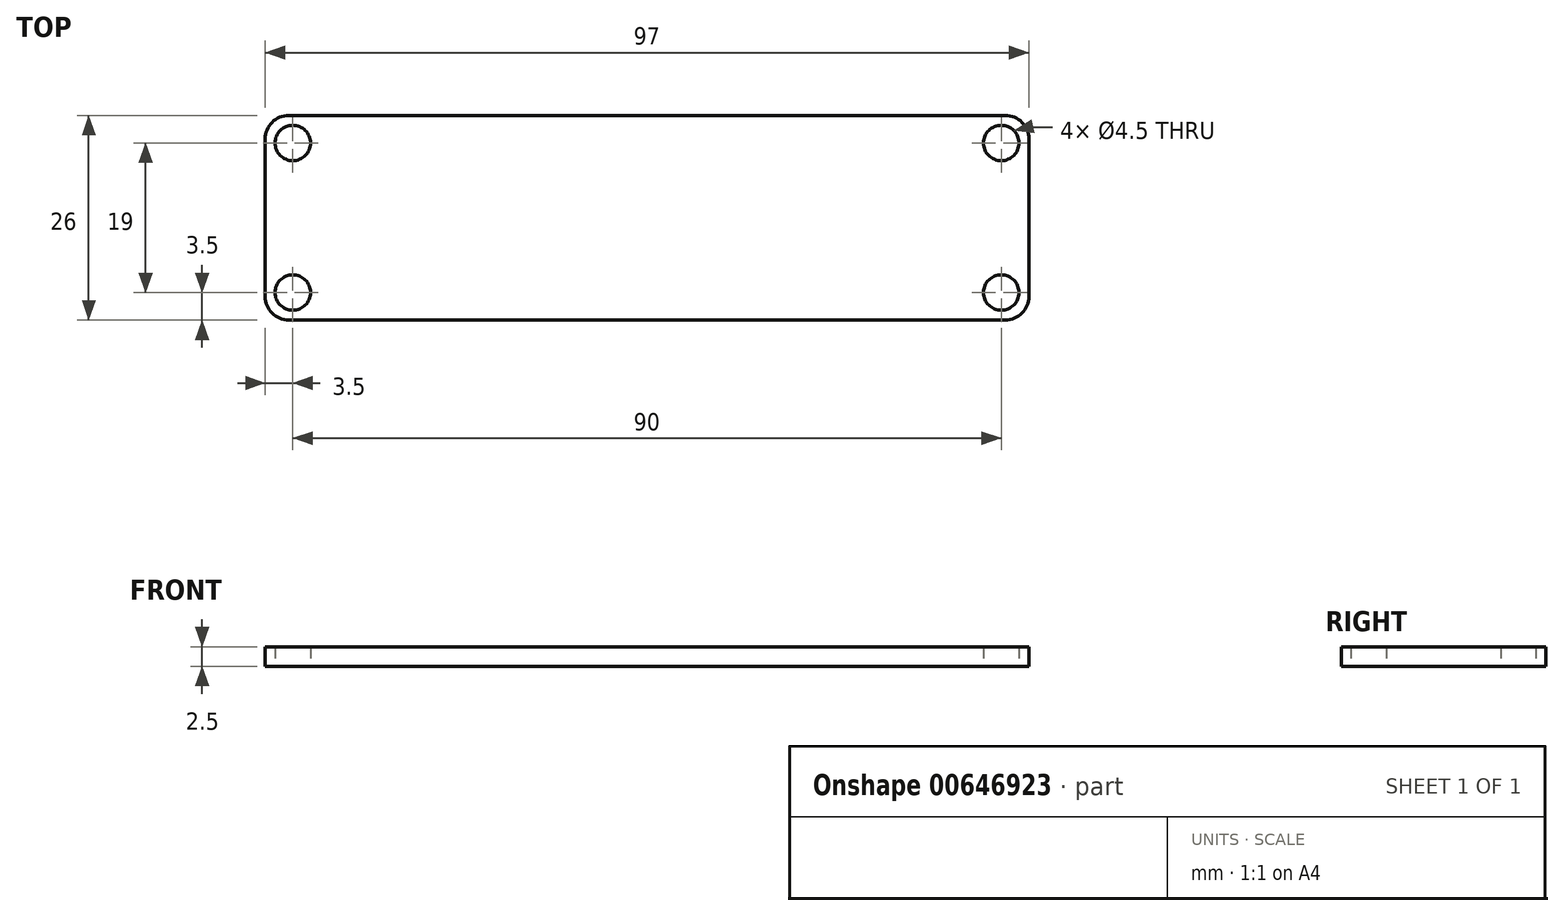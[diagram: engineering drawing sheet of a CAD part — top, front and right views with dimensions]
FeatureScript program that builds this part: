
annotation { "Feature Type Name" : "Feature", "Feature Type Description" : "" }
export const myFeature = defineFeature(function(context is Context, id is Id, definition is map)
    precondition{}
    {
        {
            var Q0;
            Q0=qCreatedBy(makeId("Top.planeOp"),FACE);
            var sketch = newSketch(context, id + "F0", { "sketchPlane" : qUnion([Q0])});
            skLineSegment(sketch, "E0.bottom", {"start": v(-45.5, 13) * mm, "end": v(45.5, 13) * mm});
            skLineSegment(sketch, "E0.top", {"start": v(-45.5, -13) * mm, "end": v(45.5, -13) * mm});
            skLineSegment(sketch, "E0.left", {"start": v(-48.5, 10) * mm, "end": v(-48.5, -10) * mm});
            skLineSegment(sketch, "E0.right", {"start": v(48.5, 10) * mm, "end": v(48.5, -10) * mm});
            skPoint(sketch, "E0.middle", {"position": v(0, 0) * mm});
            skCircle(sketch, "E1", {"center": v(-45, 9.5) * mm, "radius": 2.25 * mm});
            skCircle(sketch, "E2.MirrorC", {"center": v(45, 9.5) * mm, "radius": 2.25 * mm});
            skCircle(sketch, "E3.MirrorC", {"center": v(-45, -9.5) * mm, "radius": 2.25 * mm});
            skCircle(sketch, "E4.MirrorC", {"center": v(45, -9.5) * mm, "radius": 2.25 * mm});
            skPoint(sketch, "E5.visualSharp", {"position": v(48.5, 13) * mm});
            skArc(sketch, "E5.filletArc", {"start": v(48.5, 10) * mm, "mid": v(47.62, 12.12) * mm, "end": v(45.5, 13) * mm});
            skPoint(sketch, "E6.visualSharp", {"position": v(48.5, -13) * mm});
            skArc(sketch, "E6.filletArc", {"start": v(45.5, -13) * mm, "mid": v(47.62, -12.12) * mm, "end": v(48.5, -10) * mm});
            skPoint(sketch, "E7.visualSharp", {"position": v(-48.5, -13) * mm});
            skArc(sketch, "E7.filletArc", {"start": v(-48.5, -10) * mm, "mid": v(-47.62, -12.12) * mm, "end": v(-45.5, -13) * mm});
            skPoint(sketch, "E8.visualSharp", {"position": v(-48.5, 13) * mm});
            skArc(sketch, "E8.filletArc", {"start": v(-45.5, 13) * mm, "mid": v(-47.62, 12.12) * mm, "end": v(-48.5, 10) * mm});
            skSolve(sketch);
        }
        {
            var Q0;
            Q0=makeQuery(id+"F0.imprint","IMPRINT",FACE,{"disambiguationData":[TD([[makeQuery(id+"F0.imprint","IMPRINT",EDGE,{"derivedFrom":sQuery(id+"F0.wireOp",EDGE,"E0.bottom")}),-1.0]])]});
            extrude(context, id + "F1", {"entities" : qUnion([Q0]), "depth" : 2.5 * mm, "offsetDistance" : 25 * mm});
        }
    });
